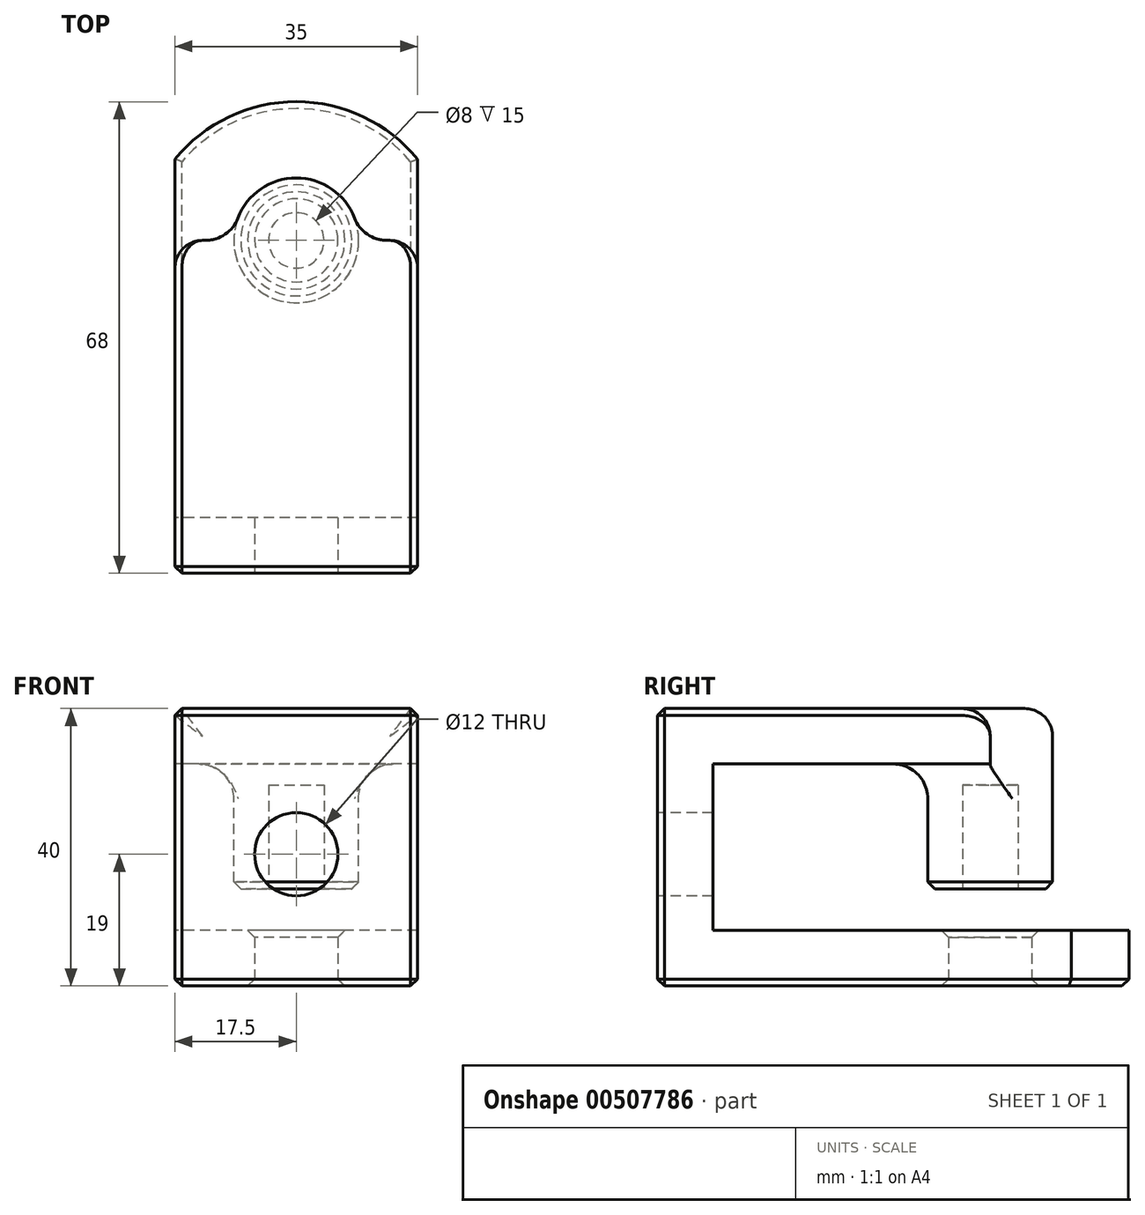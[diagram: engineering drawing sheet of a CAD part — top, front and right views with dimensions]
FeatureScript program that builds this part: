
annotation { "Feature Type Name" : "Feature", "Feature Type Description" : "" }
export const myFeature = defineFeature(function(context is Context, id is Id, definition is map)
    precondition{}
    {
        {
            var Q0;
            Q0=qCreatedBy(makeId("Top.planeOp"),FACE);
            var sketch = newSketch(context, id + "F0", { "sketchPlane" : qUnion([Q0])});
            skLineSegment(sketch, "E0.bottom", {"start": v(17.5, 25.86) * mm, "end": v(-17.5, 25.86) * mm});
            skLineSegment(sketch, "E0.top", {"start": v(17.5, -25.86) * mm, "end": v(-17.5, -25.86) * mm});
            skLineSegment(sketch, "E0.left", {"start": v(17.5, 25.86) * mm, "end": v(17.5, -25.86) * mm});
            skLineSegment(sketch, "E0.right", {"start": v(-17.5, 25.86) * mm, "end": v(-17.5, -25.86) * mm});
            skPoint(sketch, "E0.middle", {"position": v(0, 0) * mm});
            skArc(sketch, "E1", {"start": v(17.5, 25.86) * mm, "mid": v(0, 34.14) * mm, "end": v(-17.5, 25.86) * mm});
            skPoint(sketch, "E2", {"position": v(0, 34.14) * mm});
            skCircle(sketch, "E3", {"center": v(0, 14.14) * mm, "radius": 6 * mm});
            skSolve(sketch);
        }
        {
            var Q0;
            Q0=makeQuery(id+"F0.imprint","IMPRINT",FACE,{"disambiguationData":[TD([[makeQuery(id+"F0.imprint","IMPRINT",EDGE,{"derivedFrom":sQuery(id+"F0.wireOp",EDGE,"E0.bottom")}),-1.0]])]});
            var Q1;
            Q1=makeQuery(id+"F0.imprint","IMPRINT",FACE,{"disambiguationData":[TD([[makeQuery(id+"F0.imprint","IMPRINT",EDGE,{"derivedFrom":sQuery(id+"F0.wireOp",EDGE,"E0.bottom")}),1.0]])]});
            extrude(context, id + "F1", {"entities" : qUnion([Q0, Q1]), "depth" : 8 * mm, "offsetDistance" : 25 * mm});
        }
        {
            var Q0;
            Q0=makeQuery(id+"F1.opExtrude","SWEPT_FACE",FACE,{"disambiguationData":[OSD([sQuery(id+"F0.wireOp",EDGE,"E0.top")])]});
            var sketch = newSketch(context, id + "F2", { "sketchPlane" : qUnion([Q0])});
            skLineSegment(sketch, "E4.bottom", {"start": v(-17.5, 0) * mm, "end": v(17.5, 0) * mm});
            skLineSegment(sketch, "E4.top", {"start": v(-17.5, 40) * mm, "end": v(17.5, 40) * mm});
            skLineSegment(sketch, "E4.left", {"start": v(-17.5, 0) * mm, "end": v(-17.5, 40) * mm});
            skLineSegment(sketch, "E4.right", {"start": v(17.5, 0) * mm, "end": v(17.5, 40) * mm});
            skSolve(sketch);
        }
        {
            var Q0;
            Q0 = qSketchRegion(id + "F2", true);
            extrude(context, id + "F3", {"entities" : qUnion([Q0]), "operationType" : NewBodyOperationType.ADD, "depth" : 8 * mm, "offsetDistance" : 25 * mm});
        }
        {
            var Q0;
            Q0=makeQuery(id+"F3.opExtrude","CAP_FACE",FACE,{"disambiguationData":[OSD([sQuery(id+"F2.wireOp",EDGE,"E4.bottom"),sQuery(id+"F2.wireOp",EDGE,"E4.top"),sQuery(id+"F2.wireOp",EDGE,"E4.left"),sQuery(id+"F2.wireOp",EDGE,"E4.right")])],"isStart":true});
            var sketch = newSketch(context, id + "F4", { "sketchPlane" : qUnion([Q0])});
            skLineSegment(sketch, "E5.bottom", {"start": v(-17.5, 40) * mm, "end": v(17.5, 40) * mm});
            skLineSegment(sketch, "E5.top", {"start": v(-17.5, 32) * mm, "end": v(17.5, 32) * mm});
            skLineSegment(sketch, "E5.left", {"start": v(-17.5, 40) * mm, "end": v(-17.5, 32) * mm});
            skLineSegment(sketch, "E5.right", {"start": v(17.5, 40) * mm, "end": v(17.5, 32) * mm});
            skSolve(sketch);
        }
        {
            var Q0;
            Q0=makeQuery(id+"F4.imprint","IMPRINT",FACE,{"disambiguationData":[TD([[makeQuery(id+"F4.imprint","IMPRINT",EDGE,{"derivedFrom":sQuery(id+"F4.wireOp",EDGE,"E5.bottom")}),1.0]])]});
            extrude(context, id + "F5", {"entities" : qUnion([Q0]), "operationType" : NewBodyOperationType.ADD, "depth" : 40 * mm, "offsetDistance" : 25 * mm});
        }
        {
            var Q0;
            Q0=makeQuery(id+"F5.boolean.opBoolean","MERGE",FACE,{"derivedFrom":[makeQuery(id+"F3.opExtrude","SWEPT_FACE",FACE,{"disambiguationData":[OSD([sQuery(id+"F2.wireOp",EDGE,"E4.top")])]}),makeQuery(id+"F5.opExtrude","SWEPT_FACE",FACE,{"disambiguationData":[OSD([sQuery(id+"F4.wireOp",EDGE,"E5.bottom")])]})]});
            var sketch = newSketch(context, id + "F6", { "sketchPlane" : qUnion([Q0])});
            skCircle(sketch, "E6", {"center": v(0, 14.14) * mm, "radius": 9 * mm});
            skSolve(sketch);
        }
        {
            var Q0;
            {var subQ0=sQuery(id+"F6.wireOp",EDGE,"E6");var subQ1=makeQuery(id+"F5.opExtrude","CAP_EDGE",EDGE,{"disambiguationData":[OSD([sQuery(id+"F4.wireOp",EDGE,"E5.bottom")])],"isStart":false});var subQ2=makeQuery(id+"F6.imprint","INTERSECT",VERTEX,{"disambiguationData":[OD(0.0)],"derivedFrom":[subQ1,subQ0]});Q0=makeQuery(id+"F6.imprint","IMPRINT",FACE,{"disambiguationData":[TD([[makeQuery(id+"F6.imprint","IMPRINT",EDGE,{"disambiguationData":[TD([[subQ2,1.0]])],"derivedFrom":subQ0}),1.0]])]});}
            var Q1;
            {var subQ0=sQuery(id+"F6.wireOp",EDGE,"E6");var subQ1=makeQuery(id+"F5.opExtrude","CAP_EDGE",EDGE,{"disambiguationData":[OSD([sQuery(id+"F4.wireOp",EDGE,"E5.bottom")])],"isStart":false});var subQ2=makeQuery(id+"F6.imprint","INTERSECT",VERTEX,{"disambiguationData":[OD(0.0)],"derivedFrom":[subQ1,subQ0]});Q1=makeQuery(id+"F6.imprint","IMPRINT",FACE,{"disambiguationData":[TD([[makeQuery(id+"F6.imprint","IMPRINT",EDGE,{"disambiguationData":[TD([[subQ2,-1.0]])],"derivedFrom":subQ0}),1.0]])]});}
            extrude(context, id + "F7", {"entities" : qUnion([Q0, Q1]), "operationType" : NewBodyOperationType.ADD, "oppositeDirection" : true, "depth" : 26 * mm, "offsetDistance" : 25 * mm});
        }
        {
            var Q0;
            Q0=makeQuery(id+"F7.boolean.opBoolean","INTERSECT",EDGE,{"disambiguationData":[OD(1.0)],"derivedFrom":[makeQuery(id+"F5.opExtrude","CAP_FACE",FACE,{"disambiguationData":[OSD([sQuery(id+"F4.wireOp",EDGE,"E5.bottom"),sQuery(id+"F4.wireOp",EDGE,"E5.top"),sQuery(id+"F4.wireOp",EDGE,"E5.left"),sQuery(id+"F4.wireOp",EDGE,"E5.right")])],"isStart":false}),makeQuery(id+"F7.opExtrude","SWEPT_FACE",FACE,{"disambiguationData":[OSD([sQuery(id+"F6.wireOp",EDGE,"E6")])]})]});
            var Q1;
            Q1=makeQuery(id+"F7.boolean.opBoolean","INTERSECT",EDGE,{"disambiguationData":[OD(0.0)],"derivedFrom":[makeQuery(id+"F5.opExtrude","CAP_FACE",FACE,{"disambiguationData":[OSD([sQuery(id+"F4.wireOp",EDGE,"E5.bottom"),sQuery(id+"F4.wireOp",EDGE,"E5.top"),sQuery(id+"F4.wireOp",EDGE,"E5.left"),sQuery(id+"F4.wireOp",EDGE,"E5.right")])],"isStart":false}),makeQuery(id+"F7.opExtrude","SWEPT_FACE",FACE,{"disambiguationData":[OSD([sQuery(id+"F6.wireOp",EDGE,"E6")])]})]});
            var Q2;
            Q2=makeQuery(id+"F7.boolean.opBoolean","INTERSECT",EDGE,{"derivedFrom":[makeQuery(id+"F5.opExtrude","SWEPT_FACE",FACE,{"disambiguationData":[OSD([sQuery(id+"F4.wireOp",EDGE,"E5.top")])]}),makeQuery(id+"F7.opExtrude","SWEPT_FACE",FACE,{"disambiguationData":[OSD([sQuery(id+"F6.wireOp",EDGE,"E6")])]})]});
            fillet(context, id + "F8", {"entities" : qUnion([Q0, Q1, Q2]), "radius" : 5 * mm, "tangentPropagation" : true, "allowEdgeOverflow" : false});
        }
        {
            var Q0;
            Q0=makeQuery(id+"F5.opExtrude","CAP_EDGE",EDGE,{"disambiguationData":[OSD([sQuery(id+"F4.wireOp",EDGE,"E5.left")])],"isStart":false});
            var Q1;
            Q1=makeQuery(id+"F5.opExtrude","CAP_EDGE",EDGE,{"disambiguationData":[OSD([sQuery(id+"F4.wireOp",EDGE,"E5.right")])],"isStart":false});
            var Q2;
            Q2=makeQuery(id+"F5.opExtrude","CAP_EDGE",EDGE,{"disambiguationData":[OSD([sQuery(id+"F4.wireOp",EDGE,"E5.top")])],"isStart":true});
            var Q3;
            Q3=makeQuery(id+"F1.opExtrude","CAP_EDGE",EDGE,{"disambiguationData":[OSD([sQuery(id+"F0.wireOp",EDGE,"E0.top")])],"isStart":false});
            var Q4;
            Q4=makeQuery(id+"F7.opExtrude","CAP_EDGE",EDGE,{"disambiguationData":[OSD([sQuery(id+"F6.wireOp",EDGE,"E6")])],"isStart":true});
            fillet(context, id + "F9", {"entities" : qUnion([Q0, Q1, Q2, Q3, Q4]), "radius" : 4 * mm, "tangentPropagation" : true, "allowEdgeOverflow" : false});
        }
        {
            var Q0;
            Q0=makeQuery(id+"F7.opExtrude","CAP_FACE",FACE,{"disambiguationData":[OSD([sQuery(id+"F6.wireOp",EDGE,"E6")])],"isStart":false});
            var sketch = newSketch(context, id + "F10", { "sketchPlane" : qUnion([Q0])});
            skCircle(sketch, "E7", {"center": v(0, -14.14) * mm, "radius": 4 * mm});
            skSolve(sketch);
        }
        {
            var Q0;
            Q0=makeQuery(id+"F10.imprint","IMPRINT",FACE,{"disambiguationData":[TD([[makeQuery(id+"F10.imprint","IMPRINT",EDGE,{"derivedFrom":sQuery(id+"F10.wireOp",EDGE,"E7")}),1.0]])]});
            extrude(context, id + "F11", {"entities" : qUnion([Q0]), "operationType" : NewBodyOperationType.REMOVE, "oppositeDirection" : true, "depth" : 15 * mm, "offsetDistance" : 25 * mm});
        }
        {
            var Q0;
            Q0=makeQuery(id+"F11.boolean.opBoolean","COPY",EDGE,{"derivedFrom":makeQuery(id+"F11.opExtrude","CAP_EDGE",EDGE,{"disambiguationData":[OSD([sQuery(id+"F10.wireOp",EDGE,"E7")])],"isStart":true})});
            var Q1;
            Q1=makeQuery(id+"F1.opExtrude","CAP_EDGE",EDGE,{"disambiguationData":[OSD([sQuery(id+"F0.wireOp",EDGE,"E3")])],"isStart":true});
            var Q2;
            Q2=makeQuery(id+"F1.opExtrude","CAP_EDGE",EDGE,{"disambiguationData":[OSD([sQuery(id+"F0.wireOp",EDGE,"E3")])],"isStart":false});
            var Q3;
            Q3=makeQuery(id+"F7.opExtrude","CAP_EDGE",EDGE,{"disambiguationData":[OSD([sQuery(id+"F6.wireOp",EDGE,"E6")])],"isStart":false});
            var Q4;
            Q4=makeQuery(id+"F3.boolean.opBoolean","MERGE",EDGE,{"derivedFrom":[makeQuery(id+"F1.opExtrude","CAP_EDGE",EDGE,{"disambiguationData":[OSD([sQuery(id+"F0.wireOp",EDGE,"E0.right")])],"isStart":true}),makeQuery(id+"F3.opExtrude","SWEPT_EDGE",EDGE,{"disambiguationData":[OSD([sQuery(id+"F2.wireOp",EDGE,"E4.bottom"),sQuery(id+"F2.wireOp",EDGE,"E4.left")])]})]});
            var Q5;
            Q5=makeQuery(id+"F1.opExtrude","CAP_EDGE",EDGE,{"disambiguationData":[OSD([sQuery(id+"F0.wireOp",EDGE,"E1")])],"isStart":true});
            var Q6;
            Q6=makeQuery(id+"F3.boolean.opBoolean","MERGE",EDGE,{"derivedFrom":[makeQuery(id+"F1.opExtrude","CAP_EDGE",EDGE,{"disambiguationData":[OSD([sQuery(id+"F0.wireOp",EDGE,"E0.left")])],"isStart":true}),makeQuery(id+"F3.opExtrude","SWEPT_EDGE",EDGE,{"disambiguationData":[OSD([sQuery(id+"F2.wireOp",EDGE,"E4.bottom"),sQuery(id+"F2.wireOp",EDGE,"E4.right")])]})]});
            var Q7;
            Q7=makeQuery(id+"F3.opExtrude","CAP_EDGE",EDGE,{"disambiguationData":[OSD([sQuery(id+"F2.wireOp",EDGE,"E4.bottom")])],"isStart":false});
            var Q8;
            Q8=makeQuery(id+"F3.opExtrude","CAP_EDGE",EDGE,{"disambiguationData":[OSD([sQuery(id+"F2.wireOp",EDGE,"E4.left")])],"isStart":false});
            var Q9;
            Q9=makeQuery(id+"F5.boolean.opBoolean","MERGE",EDGE,{"derivedFrom":[makeQuery(id+"F3.opExtrude","SWEPT_EDGE",EDGE,{"disambiguationData":[OSD([sQuery(id+"F2.wireOp",EDGE,"E4.top"),sQuery(id+"F2.wireOp",EDGE,"E4.left")])]}),makeQuery(id+"F5.opExtrude","SWEPT_EDGE",EDGE,{"disambiguationData":[OSD([sQuery(id+"F4.wireOp",EDGE,"E5.bottom"),sQuery(id+"F4.wireOp",EDGE,"E5.right")])]})]});
            var Q10;
            Q10=makeQuery(id+"F5.boolean.opBoolean","MERGE",EDGE,{"derivedFrom":[makeQuery(id+"F3.opExtrude","SWEPT_EDGE",EDGE,{"disambiguationData":[OSD([sQuery(id+"F2.wireOp",EDGE,"E4.top"),sQuery(id+"F2.wireOp",EDGE,"E4.right")])]}),makeQuery(id+"F5.opExtrude","SWEPT_EDGE",EDGE,{"disambiguationData":[OSD([sQuery(id+"F4.wireOp",EDGE,"E5.bottom"),sQuery(id+"F4.wireOp",EDGE,"E5.left")])]})]});
            var Q11;
            Q11=makeQuery(id+"F3.opExtrude","CAP_EDGE",EDGE,{"disambiguationData":[OSD([sQuery(id+"F2.wireOp",EDGE,"E4.top")])],"isStart":false});
            var Q12;
            Q12=makeQuery(id+"F3.opExtrude","CAP_EDGE",EDGE,{"disambiguationData":[OSD([sQuery(id+"F2.wireOp",EDGE,"E4.right")])],"isStart":false});
            chamfer(context, id + "F12", {"entities" : qUnion([Q0, Q1, Q2, Q3, Q4, Q5, Q6, Q7, Q8, Q9, Q10, Q11, Q12]), "width" : 1 * mm, "tangentPropagation" : true});
        }
        {
            var Q0;
            Q0=makeQuery(id+"F3.opExtrude","CAP_FACE",FACE,{"disambiguationData":[OSD([sQuery(id+"F2.wireOp",EDGE,"E4.bottom"),sQuery(id+"F2.wireOp",EDGE,"E4.top"),sQuery(id+"F2.wireOp",EDGE,"E4.left"),sQuery(id+"F2.wireOp",EDGE,"E4.right")])],"isStart":false});
            var sketch = newSketch(context, id + "F13", { "sketchPlane" : qUnion([Q0])});
            skCircle(sketch, "E8", {"center": v(0, 19) * mm, "radius": 6 * mm});
            skSolve(sketch);
        }
        {
            var Q0;
            Q0=makeQuery(id+"F13.imprint","IMPRINT",FACE,{"disambiguationData":[TD([[makeQuery(id+"F13.imprint","IMPRINT",EDGE,{"derivedFrom":sQuery(id+"F13.wireOp",EDGE,"E8")}),1.0]])]});
            extrude(context, id + "F14", {"entities" : qUnion([Q0]), "operationType" : NewBodyOperationType.REMOVE, "oppositeDirection" : true, "depth" : 25 * mm, "offsetDistance" : 25 * mm});
        }
    });
